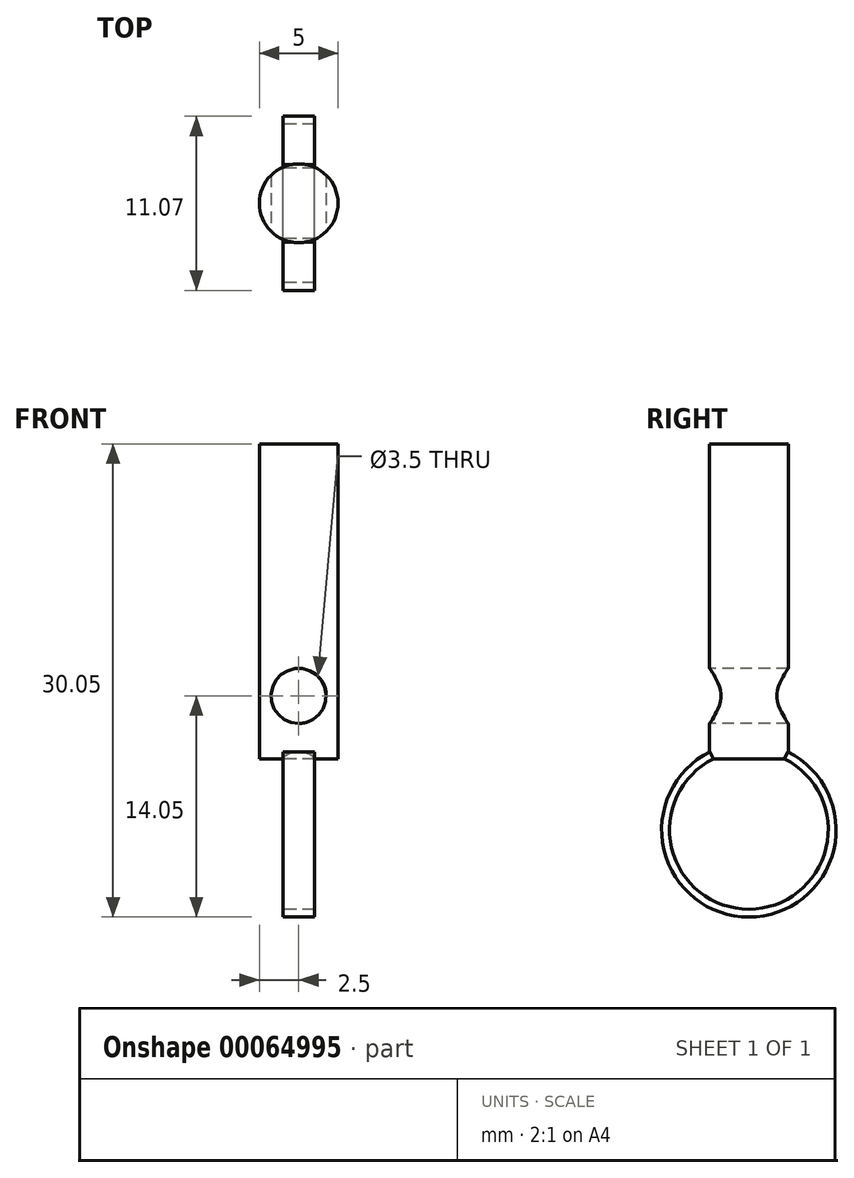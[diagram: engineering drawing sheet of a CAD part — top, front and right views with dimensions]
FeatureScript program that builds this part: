
annotation { "Feature Type Name" : "Feature", "Feature Type Description" : "" }
export const myFeature = defineFeature(function(context is Context, id is Id, definition is map)
    precondition{}
    {
        {
            var Q0;
            Q0=qCreatedBy(makeId("Front.planeOp"),FACE);
            var sketch = newSketch(context, id + "F0", { "sketchPlane" : qUnion([Q0])});
            skLineSegment(sketch, "E0.bottom", {"start": v(0, 0) * mm, "end": v(-2.5, 0) * mm});
            skLineSegment(sketch, "E0.top", {"start": v(0, 20) * mm, "end": v(-2.5, 20) * mm});
            skLineSegment(sketch, "E0.left", {"start": v(0, 0) * mm, "end": v(0, 20) * mm});
            skLineSegment(sketch, "E0.right", {"start": v(-2.5, 0) * mm, "end": v(-2.5, 20) * mm});
            skSolve(sketch);
        }
        {
            var Q0;
            Q0 = qSketchRegion(id + "F0", true);
            var Q1;
            Q1=sQuery(id+"F0.wireOp",EDGE,"E0.left");
            revolve(context, id + "F1", {"entities" : qUnion([Q0]), "axis" : qUnion([Q1]), "revolveType" : RevolveType.FULL});
        }
        {
            var Q0;
            Q0=qCreatedBy(makeId("Front.planeOp"),FACE);
            var sketch = newSketch(context, id + "F2", { "sketchPlane" : qUnion([Q0])});
            skCircle(sketch, "E1", {"center": v(0, 4) * mm, "radius": 1.75 * mm});
            skSolve(sketch);
        }
        {
            var Q0;
            Q0 = qSketchRegion(id + "F2", true);
            extrude(context, id + "F3", {"entities" : qUnion([Q0]), "operationType" : NewBodyOperationType.REMOVE, "endBound" : BoundingType.SYMMETRIC, "oppositeDirection" : true, "depth" : 5 * mm});
        }
        {
            var Q0;
            Q0=qCreatedBy(makeId("Right.planeOp"),FACE);
            var sketch = newSketch(context, id + "F4", { "sketchPlane" : qUnion([Q0])});
            skArc(sketch, "E2", {"start": v(-2.26, 0) * mm, "mid": v(0, -9.55) * mm, "end": v(2.24, 0) * mm});
            skArc(sketch, "E3.0", {"start": v(-2.48, 0.45) * mm, "mid": v(0, -10.05) * mm, "end": v(2.47, 0.45) * mm});
            skLineSegment(sketch, "E4", {"start": v(-2.48, 0.45) * mm, "end": v(-2.26, 0) * mm});
            skLineSegment(sketch, "E5", {"start": v(2.47, 0.45) * mm, "end": v(2.24, 0) * mm});
            skSolve(sketch);
        }
        {
            var Q0;
            Q0 = qSketchRegion(id + "F4", true);
            extrude(context, id + "F5", {"entities" : qUnion([Q0]), "operationType" : NewBodyOperationType.ADD, "endBound" : BoundingType.SYMMETRIC, "depth" : 2 * mm});
        }
    });
